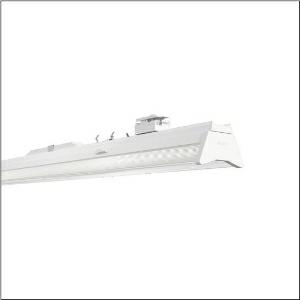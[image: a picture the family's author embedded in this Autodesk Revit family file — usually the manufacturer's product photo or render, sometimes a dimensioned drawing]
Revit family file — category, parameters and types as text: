
# Revit family: licross_r__11_performance_ho_51td16dn6exm_746f
name_source: partatom
category: Lighting Fixtures
units: mm (PartAtom-declared; Revit-internal decimal feet)

## family parameters
Cut with Voids When Loaded = No
Host = Face
Light Source = No
Part Type = Normal
Room Calculation Point = No
Round Connector Dimension = Use Diameter
Shared = No

## types (1)
- --- (1 x LED, 14180 lm, 81.4 W, 6500K)
    Apparent Load = 81 VA
    CIE Flux Codes = 63 87 95 78 100
    Color Rendering = 80
    Color Temperature = 6500K
    Default Elevation = 1800 mm
    Description = Licross® 11 Performance HO, luminaire insert, of sheet steel, galvanised, coil coated, white, length: 1.500mm, width: 120mm, height: 123mm, LED rated luminous flux: 14.180lm, light colour: 865, control gear: DALI 2, with plug, 5-pole, with phase selection, mains connection: 220..240V, AC, 50/60Hz, rated input power: 81W, internal wiring halogen-free, primary light control with lens, of plastic, primary optical cover: cover, of PMMA, light emission: direct/indirect distribution, primary light characteristic: symmetric, protection rating (complete): IP54, insulation class (complete): insulation class I (protective earthing), certification: CE, ENEC, VDE, UKCA, protection symbol: D if used in an environment with non-conductive dust loads with corresponding accessories, impact resistance: IK06, permissible ambient temperature for indoor applications: -25..+35°C, corresponds to IFS (International Featured Standards) requirements for safety and quality in the food industry, reducing of maximum allowable ambient temperature of 5°C with ceiling mounting, LABS conformity tested according to VDMA 24364:2018-05, packaging unit: 1 piece
    Height = 114 mm
    Lamp = 1 x LED
    Lamp Light Flux = 14180 lm
    Lamp Power = 81.4 W
    Lamp count = 1
    Length = 1500 mm
    Luminous efficacy = 174 lm/W
    Manufacturer = Siteco
    ModVariant = No
    Model = 51TD16DN6EXM
    Mounting Place = Ceiling
    Mounting Type = Pendant
    Number of Poles = 1
    OnlyDefault = Yes
    Power Factor = 1
    Product Name = Licross® 11 Performance HO
    Product group = luminaire insert | ceiling pendant
    ProductGroupID = 902
    Protection Class = Protection class I
    Protection Degree = IP 54
    RLX_Detail_Level = 1
    RLX_Emergency_Light_Flux = 0 lm
    RLX_Emergency_Type = 0
    RLX_Emergency_Type_DB = No
    RlxData = <blob elided: 34161 chars, md5=87e133ea>
    Socket = socket
    Standby Power = 0 W
    System Light Flux = 14180 lm
    System Power = 81 W
    Type Comments = factory setting: luminous flux: 100 % | dim-lin: 254 | 550 mA
    Type Image = l_1256138.jpg
    URL = http://relux.com
    VarID = @adj_089501
    Voltage = 0 V
    Weight = 0.00 kg
    Width = 120 mm

## geometry (parser evidence)
native form markers: Blend x4, Sweep x13
no freeform markers — native parametric forms only
